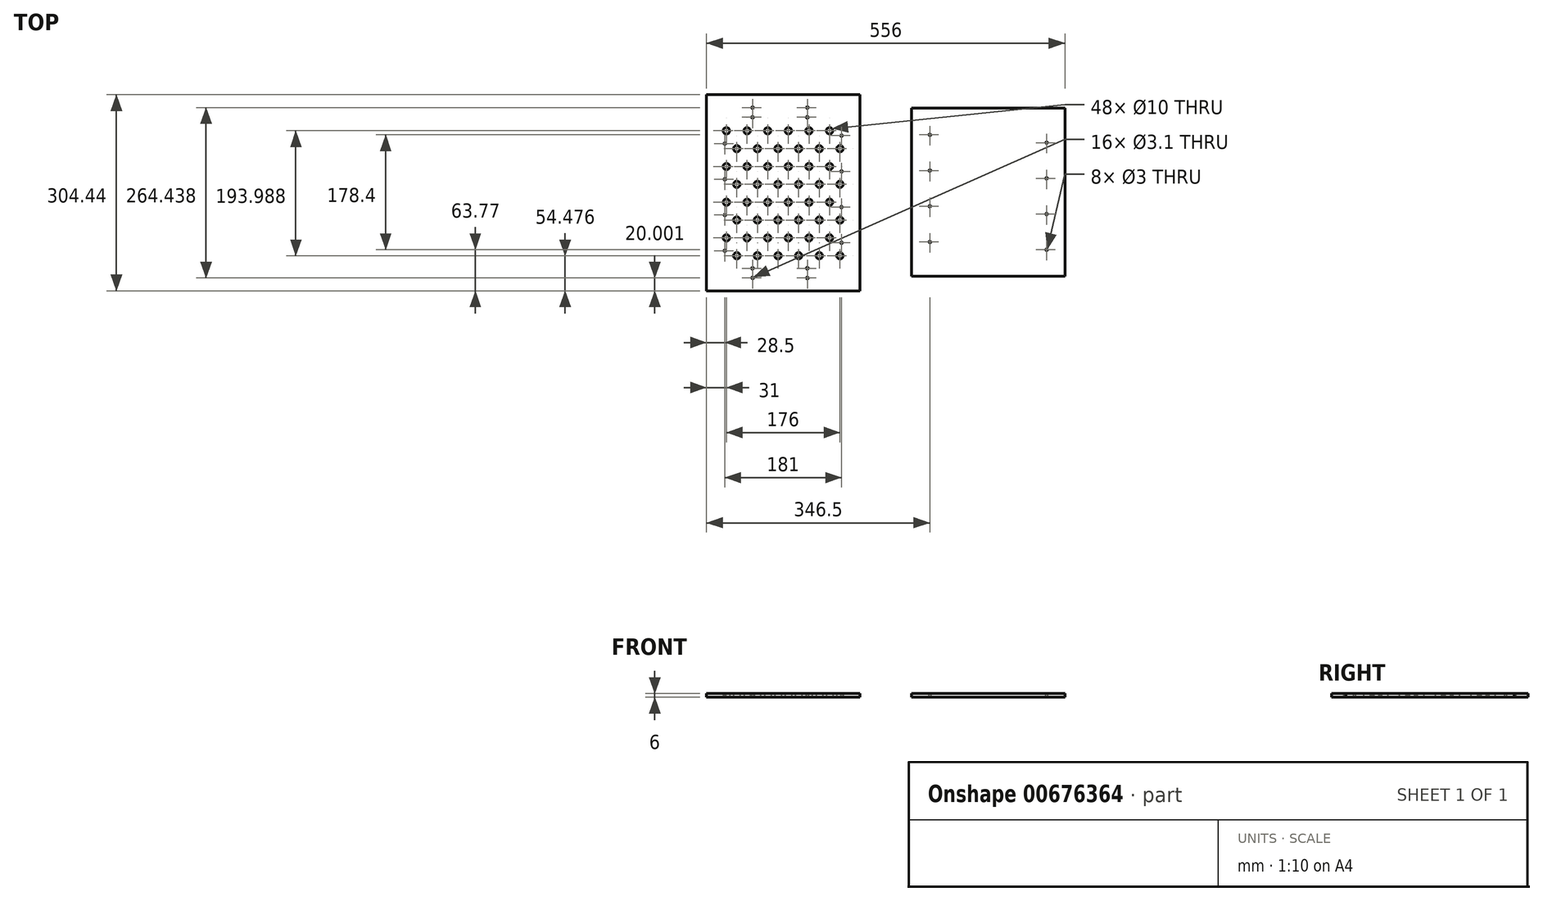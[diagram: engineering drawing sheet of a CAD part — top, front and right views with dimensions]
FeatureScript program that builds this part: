
annotation { "Feature Type Name" : "Feature", "Feature Type Description" : "" }
export const myFeature = defineFeature(function(context is Context, id is Id, definition is map)
    precondition{}
    {
        {
            var Q0;
            Q0=qCreatedBy(makeId("Top.planeOp"),FACE);
            var sketch = newSketch(context, id + "F0", { "sketchPlane" : qUnion([Q0])});
            skLineSegment(sketch, "E0.bottom", {"start": v(119, -130.47) * mm, "end": v(-119, -130.47) * mm});
            skLineSegment(sketch, "E0.top", {"start": v(119, 130.47) * mm, "end": v(-119, 130.47) * mm});
            skLineSegment(sketch, "E0.left", {"start": v(119, -130.47) * mm, "end": v(119, 130.47) * mm});
            skLineSegment(sketch, "E0.right", {"start": v(-119, -130.47) * mm, "end": v(-119, 130.47) * mm});
            skPoint(sketch, "E0.middle", {"position": v(0, 0) * mm});
            skCircle(sketch, "E1", {"center": v(-90.5, -77.08) * mm, "radius": 1.5 * mm});
            skCircle(sketch, "E2", {"center": v(-90.5, -21.65) * mm, "radius": 1.5 * mm});
            skCircle(sketch, "E3", {"center": v(90.5, -89.2) * mm, "radius": 1.5 * mm});
            skCircle(sketch, "E4", {"center": v(90.5, -33.77) * mm, "radius": 1.5 * mm});
            skPoint(sketch, "E5.endSnap0", {"position": v(0, 130.47) * mm});
            skCircle(sketch, "E6.0.1.0", {"center": v(-90.5, 33.77) * mm, "radius": 1.5 * mm});
            skCircle(sketch, "E6.0.2.0", {"center": v(-90.5, 89.2) * mm, "radius": 1.5 * mm});
            skLineSegment(sketch, "E6.direction1", {"start": v(-90.5, -21.65) * mm, "end": v(-65.5, -21.65) * mm, "construction": true});
            skLineSegment(sketch, "E6.direction2", {"start": v(-90.5, -21.65) * mm, "end": v(-90.5, 33.77) * mm, "construction": true});
            skCircle(sketch, "E7.0.1.0", {"center": v(90.5, 21.65) * mm, "radius": 1.5 * mm});
            skLineSegment(sketch, "E7.direction1", {"start": v(90.5, -33.77) * mm, "end": v(115.5, -33.77) * mm, "construction": true});
            skLineSegment(sketch, "E7.direction2", {"start": v(90.5, -33.77) * mm, "end": v(90.5, 21.65) * mm, "construction": true});
            skCircle(sketch, "E8.0.0.2", {"center": v(90.5, 77.08) * mm, "radius": 1.5 * mm});
            skLineSegment(sketch, "E9", {"start": v(-159, 130.47) * mm, "end": v(-159, 100.47) * mm, "construction": true});
            skPoint(sketch, "E10.MirrorP", {"position": v(-318, 0) * mm});
            skLineSegment(sketch, "E11.MirrorCS", {"start": v(-199, -130.47) * mm, "end": v(-199, 130.47) * mm});
            skLineSegment(sketch, "E12.MirrorCS", {"start": v(-437, -130.47) * mm, "end": v(-437, 130.47) * mm});
            skLineSegment(sketch, "E13", {"start": v(-437, 130.47) * mm, "end": v(-437, 151.47) * mm});
            skLineSegment(sketch, "E14", {"start": v(-437, 151.47) * mm, "end": v(-199, 151.47) * mm});
            skLineSegment(sketch, "E15", {"start": v(-199, 151.47) * mm, "end": v(-199, 130.47) * mm});
            skLineSegment(sketch, "E16", {"start": v(-437, -130.47) * mm, "end": v(-437, -152.97) * mm});
            skLineSegment(sketch, "E17", {"start": v(-437, -152.97) * mm, "end": v(-199, -152.97) * mm});
            skLineSegment(sketch, "E18", {"start": v(-199, -152.97) * mm, "end": v(-199, -130.47) * mm});
            skLineSegment(sketch, "E19", {"start": v(-437, 130.47) * mm, "end": v(-199, 130.47) * mm, "construction": true});
            skLineSegment(sketch, "E20", {"start": v(-437, -130.47) * mm, "end": v(-199, -130.47) * mm, "construction": true});
            skPoint(sketch, "E21", {"position": v(-406, -70.78) * mm});
            skPoint(sketch, "E22", {"position": v(-390, -98.5) * mm});
            skCircle(sketch, "E23", {"center": v(-406, -70.78) * mm, "radius": 5 * mm});
            skCircle(sketch, "E24", {"center": v(-390, -98.5) * mm, "radius": 5 * mm});
            skCircle(sketch, "E25.1.0.0", {"center": v(-358, -98.5) * mm, "radius": 5 * mm});
            skCircle(sketch, "E25.1.0.1", {"center": v(-374, -70.78) * mm, "radius": 5 * mm});
            skCircle(sketch, "E25.2.0.0", {"center": v(-326, -98.5) * mm, "radius": 5 * mm});
            skCircle(sketch, "E25.2.0.1", {"center": v(-342, -70.78) * mm, "radius": 5 * mm});
            skCircle(sketch, "E25.3.0.0", {"center": v(-294, -98.5) * mm, "radius": 5 * mm});
            skCircle(sketch, "E25.3.0.1", {"center": v(-310, -70.78) * mm, "radius": 5 * mm});
            skCircle(sketch, "E25.4.0.0", {"center": v(-262, -98.5) * mm, "radius": 5 * mm});
            skCircle(sketch, "E25.4.0.1", {"center": v(-278, -70.78) * mm, "radius": 5 * mm});
            skCircle(sketch, "E25.5.0.0", {"center": v(-230, -98.5) * mm, "radius": 5 * mm});
            skCircle(sketch, "E25.5.0.1", {"center": v(-246, -70.78) * mm, "radius": 5 * mm});
            skLineSegment(sketch, "E25.direction1", {"start": v(-390, -98.5) * mm, "end": v(-358, -98.5) * mm, "construction": true});
            skCircle(sketch, "E26.0.1.0", {"center": v(-390, -43.07) * mm, "radius": 5 * mm});
            skCircle(sketch, "E26.0.1.1", {"center": v(-342, -15.36) * mm, "radius": 5 * mm});
            skCircle(sketch, "E26.0.1.2", {"center": v(-246, -15.36) * mm, "radius": 5 * mm});
            skCircle(sketch, "E26.0.1.3", {"center": v(-358, -43.07) * mm, "radius": 5 * mm});
            skPoint(sketch, "E26.0.1.4", {"position": v(-406, -15.36) * mm});
            skCircle(sketch, "E26.0.1.5", {"center": v(-294, -43.07) * mm, "radius": 5 * mm});
            skCircle(sketch, "E26.0.1.6", {"center": v(-310, -15.36) * mm, "radius": 5 * mm});
            skLineSegment(sketch, "E26.0.1.7", {"start": v(-390, -43.07) * mm, "end": v(-358, -43.07) * mm, "construction": true});
            skCircle(sketch, "E26.0.1.8", {"center": v(-278, -15.36) * mm, "radius": 5 * mm});
            skCircle(sketch, "E26.0.1.9", {"center": v(-230, -43.07) * mm, "radius": 5 * mm});
            skCircle(sketch, "E26.0.1.10", {"center": v(-406, -15.36) * mm, "radius": 5 * mm});
            skPoint(sketch, "E26.0.1.11", {"position": v(-390, -43.07) * mm});
            skCircle(sketch, "E26.0.1.12", {"center": v(-374, -15.36) * mm, "radius": 5 * mm});
            skCircle(sketch, "E26.0.1.13", {"center": v(-326, -43.07) * mm, "radius": 5 * mm});
            skCircle(sketch, "E26.0.1.14", {"center": v(-262, -43.07) * mm, "radius": 5 * mm});
            skCircle(sketch, "E26.0.2.0", {"center": v(-390, 12.36) * mm, "radius": 5 * mm});
            skCircle(sketch, "E26.0.2.1", {"center": v(-342, 40.07) * mm, "radius": 5 * mm});
            skCircle(sketch, "E26.0.2.2", {"center": v(-246, 40.07) * mm, "radius": 5 * mm});
            skCircle(sketch, "E26.0.2.3", {"center": v(-358, 12.36) * mm, "radius": 5 * mm});
            skPoint(sketch, "E26.0.2.4", {"position": v(-406, 40.07) * mm});
            skCircle(sketch, "E26.0.2.5", {"center": v(-294, 12.36) * mm, "radius": 5 * mm});
            skCircle(sketch, "E26.0.2.6", {"center": v(-310, 40.07) * mm, "radius": 5 * mm});
            skLineSegment(sketch, "E26.0.2.7", {"start": v(-390, 12.36) * mm, "end": v(-358, 12.36) * mm, "construction": true});
            skCircle(sketch, "E26.0.2.8", {"center": v(-278, 40.07) * mm, "radius": 5 * mm});
            skCircle(sketch, "E26.0.2.9", {"center": v(-230, 12.36) * mm, "radius": 5 * mm});
            skCircle(sketch, "E26.0.2.10", {"center": v(-406, 40.07) * mm, "radius": 5 * mm});
            skPoint(sketch, "E26.0.2.11", {"position": v(-390, 12.36) * mm});
            skCircle(sketch, "E26.0.2.12", {"center": v(-374, 40.07) * mm, "radius": 5 * mm});
            skCircle(sketch, "E26.0.2.13", {"center": v(-326, 12.36) * mm, "radius": 5 * mm});
            skCircle(sketch, "E26.0.2.14", {"center": v(-262, 12.36) * mm, "radius": 5 * mm});
            skCircle(sketch, "E26.0.3.0", {"center": v(-390, 67.78) * mm, "radius": 5 * mm});
            skCircle(sketch, "E26.0.3.1", {"center": v(-342, 95.5) * mm, "radius": 5 * mm});
            skCircle(sketch, "E26.0.3.2", {"center": v(-246, 95.5) * mm, "radius": 5 * mm});
            skCircle(sketch, "E26.0.3.3", {"center": v(-358, 67.78) * mm, "radius": 5 * mm});
            skPoint(sketch, "E26.0.3.4", {"position": v(-406, 95.5) * mm});
            skCircle(sketch, "E26.0.3.5", {"center": v(-294, 67.78) * mm, "radius": 5 * mm});
            skCircle(sketch, "E26.0.3.6", {"center": v(-310, 95.5) * mm, "radius": 5 * mm});
            skLineSegment(sketch, "E26.0.3.7", {"start": v(-390, 67.78) * mm, "end": v(-358, 67.78) * mm, "construction": true});
            skCircle(sketch, "E26.0.3.8", {"center": v(-278, 95.5) * mm, "radius": 5 * mm});
            skCircle(sketch, "E26.0.3.9", {"center": v(-230, 67.78) * mm, "radius": 5 * mm});
            skCircle(sketch, "E26.0.3.10", {"center": v(-406, 95.5) * mm, "radius": 5 * mm});
            skPoint(sketch, "E26.0.3.11", {"position": v(-390, 67.78) * mm});
            skCircle(sketch, "E26.0.3.12", {"center": v(-374, 95.5) * mm, "radius": 5 * mm});
            skCircle(sketch, "E26.0.3.13", {"center": v(-326, 67.78) * mm, "radius": 5 * mm});
            skCircle(sketch, "E26.0.3.14", {"center": v(-262, 67.78) * mm, "radius": 5 * mm});
            skLineSegment(sketch, "E26.direction1", {"start": v(-390, -98.5) * mm, "end": v(-365, -98.5) * mm, "construction": true});
            skLineSegment(sketch, "E26.direction2", {"start": v(-390, -98.5) * mm, "end": v(-390, -43.07) * mm, "construction": true});
            skCircle(sketch, "E27", {"center": v(-280.5, 131.47) * mm, "radius": 1.55 * mm});
            skCircle(sketch, "E28", {"center": v(-280.5, 116.47) * mm, "radius": 1.55 * mm});
            skCircle(sketch, "E29", {"center": v(-365.5, 131.47) * mm, "radius": 1.55 * mm});
            skCircle(sketch, "E30", {"center": v(-365.5, 116.47) * mm, "radius": 1.55 * mm});
            skCircle(sketch, "E31", {"center": v(-365.5, -132.97) * mm, "radius": 1.55 * mm});
            skCircle(sketch, "E32", {"center": v(-365.5, -117.97) * mm, "radius": 1.55 * mm});
            skCircle(sketch, "E33", {"center": v(-280.5, -132.97) * mm, "radius": 1.55 * mm});
            skCircle(sketch, "E34", {"center": v(-280.5, -117.97) * mm, "radius": 1.55 * mm});
            skCircle(sketch, "E35", {"center": v(-408.5, 75.57) * mm, "radius": 1.55 * mm});
            skCircle(sketch, "E36", {"center": v(-227.5, 87.95) * mm, "radius": 1.55 * mm});
            skCircle(sketch, "E37.0.1.0", {"center": v(-408.5, 20.15) * mm, "radius": 1.55 * mm});
            skCircle(sketch, "E37.0.1.1", {"center": v(-227.5, 32.52) * mm, "radius": 1.55 * mm});
            skCircle(sketch, "E37.0.2.0", {"center": v(-408.5, -35.28) * mm, "radius": 1.55 * mm});
            skCircle(sketch, "E37.0.2.1", {"center": v(-227.5, -22.9) * mm, "radius": 1.55 * mm});
            skCircle(sketch, "E37.0.3.0", {"center": v(-408.5, -90.7) * mm, "radius": 1.55 * mm});
            skCircle(sketch, "E37.0.3.1", {"center": v(-227.5, -78.33) * mm, "radius": 1.55 * mm});
            skLineSegment(sketch, "E37.direction1", {"start": v(-408.5, 75.57) * mm, "end": v(-383.5, 75.57) * mm, "construction": true});
            skLineSegment(sketch, "E37.direction2", {"start": v(-408.5, 75.57) * mm, "end": v(-408.5, 20.15) * mm, "construction": true});
            skSolve(sketch);
        }
        {
            var Q0;
            Q0 = qSketchRegion(id + "F0", true);
            extrude(context, id + "F1", {"entities" : qUnion([Q0]), "depth" : 6 * mm, "offsetDistance" : 25 * mm});
        }
    });
